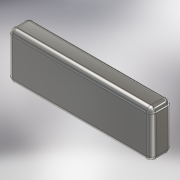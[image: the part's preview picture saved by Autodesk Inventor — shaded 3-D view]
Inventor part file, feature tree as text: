
AUTODESK INVENTOR PART (.ipt)
format: ipt  version: 2018 (Build 220112000, 112)  size: 133,120 bytes
history: native  units: mm
features: extrude x1, fillet x1, sketch x1
ambient origin geometry x8: Origin, YZ Plane, XZ Plane, XY Plane, X Axis, Y Axis, Z Axis, Center Point
bodies: Solid1 (feature_tree)
feature tree (3):
  extrude  "Extrusion1"  Depth=9.5mm
  fillet  "Fillet1"  Radius=4.3mm
  sketch  "Sketch1"  dims[d0=29.0mm d1=9.5mm d2=4.3mm d3=0.0mm d4=1.0mm]
